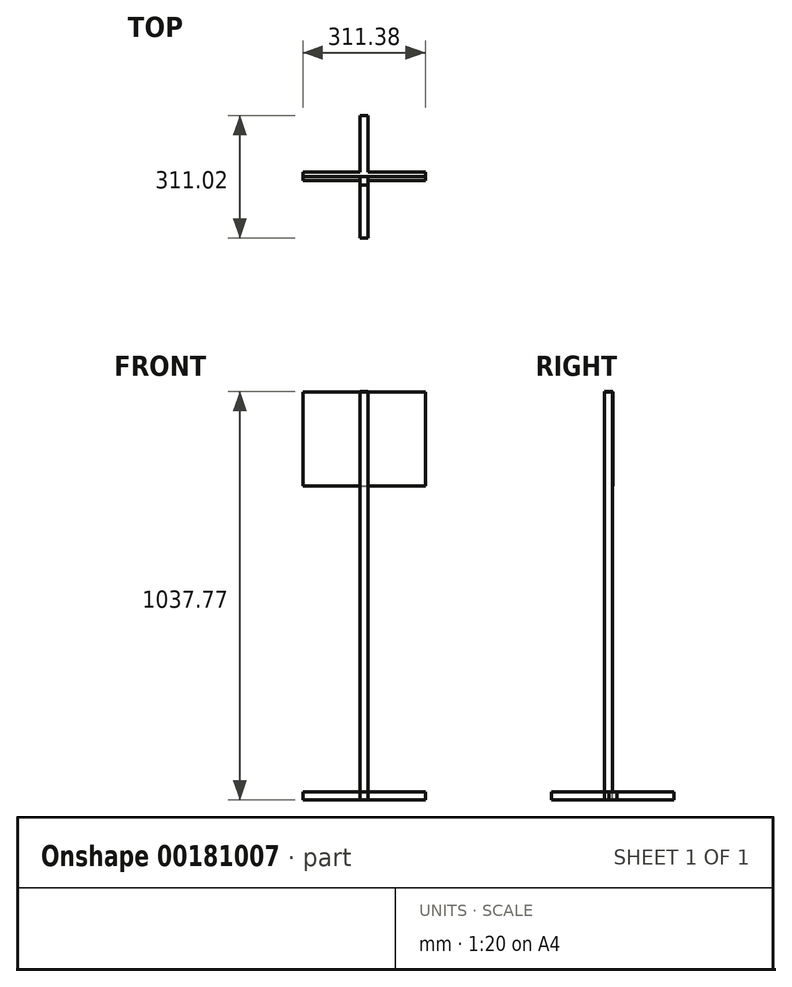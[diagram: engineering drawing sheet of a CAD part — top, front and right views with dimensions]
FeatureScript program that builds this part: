
annotation { "Feature Type Name" : "Feature", "Feature Type Description" : "" }
export const myFeature = defineFeature(function(context is Context, id is Id, definition is map)
    precondition{}
    {
        {
            var Q0;
            Q0=qCreatedBy(makeId("Front.planeOp"),FACE);
            var sketch = newSketch(context, id + "F0", { "sketchPlane" : qUnion([Q0])});
            skLineSegment(sketch, "E0.bottom", {"start": v(-155.15, 132.26) * mm, "end": v(155.87, 132.26) * mm});
            skLineSegment(sketch, "E0.top", {"start": v(-155.15, -106.2) * mm, "end": v(155.87, -106.2) * mm});
            skLineSegment(sketch, "E0.left", {"start": v(-155.15, 132.26) * mm, "end": v(-155.15, -106.2) * mm});
            skLineSegment(sketch, "E0.right", {"start": v(155.87, 132.26) * mm, "end": v(155.87, -106.2) * mm});
            skSolve(sketch);
        }
        {
            var Q0;
            Q0=makeQuery(id+"F0.imprint","IMPRINT",FACE,{"disambiguationData":[TD([[makeQuery(id+"F0.imprint","IMPRINT",EDGE,{"derivedFrom":sQuery(id+"F0.wireOp",EDGE,"E0.bottom")}),-1.0]])]});
            extrude(context, id + "F1", {"entities" : qUnion([Q0]), "depth" : 1 * mm});
        }
        {
            var Q0;
            Q0=makeQuery(id+"F1.opExtrude","CAP_FACE",FACE,{"disambiguationData":[OSD([sQuery(id+"F0.wireOp",EDGE,"E0.bottom"),sQuery(id+"F0.wireOp",EDGE,"E0.top"),sQuery(id+"F0.wireOp",EDGE,"E0.left"),sQuery(id+"F0.wireOp",EDGE,"E0.right")])],"isStart":false});
            var sketch = newSketch(context, id + "F2", { "sketchPlane" : qUnion([Q0])});
            skLineSegment(sketch, "E1.bottom", {"start": v(-10.37, 131.22) * mm, "end": v(10.37, 131.22) * mm});
            skLineSegment(sketch, "E1.top", {"start": v(-10.37, 133.3) * mm, "end": v(10.37, 133.3) * mm});
            skLineSegment(sketch, "E1.left", {"start": v(-10.37, 131.22) * mm, "end": v(-10.37, 133.3) * mm});
            skLineSegment(sketch, "E1.right", {"start": v(10.37, 131.22) * mm, "end": v(10.37, 133.3) * mm});
            skPoint(sketch, "E1.middle", {"position": v(0, 132.26) * mm});
            skSolve(sketch);
        }
        {
            var Q0;
            {var subQ0=sQuery(id+"F2.wireOp",EDGE,"E1.top");Q0=makeQuery(id+"F2.imprint","IMPRINT",FACE,{"disambiguationData":[TD([[makeQuery(id+"F2.imprint","IMPRINT",EDGE,{"derivedFrom":subQ0}),-1.0]])]});}
            extrude(context, id + "F3", {"entities" : qUnion([Q0]), "operationType" : NewBodyOperationType.ADD, "depth" : 20.73 * mm});
        }
        {
            var Q0;
            Q0=makeQuery(id+"F3.opExtrude","SWEPT_FACE",FACE,{"disambiguationData":[OSD([sQuery(id+"F0.wireOp",EDGE,"E0.bottom")])]});
            var sketch = newSketch(context, id + "F4", { "sketchPlane" : qUnion([Q0])});
            skLineSegment(sketch, "E2", {"start": v(-10.37, 21.73) * mm, "end": v(10.37, 21.73) * mm});
            skLineSegment(sketch, "E3", {"start": v(10.37, 21.73) * mm, "end": v(10.37, 1) * mm});
            skLineSegment(sketch, "E4", {"start": v(10.37, 1) * mm, "end": v(-10.37, 1) * mm});
            skLineSegment(sketch, "E5", {"start": v(-10.37, 1) * mm, "end": v(-10.37, 21.73) * mm});
            skSolve(sketch);
        }
        {
            var Q0;
            Q0=makeQuery(id+"F1.opExtrude","CAP_FACE",FACE,{"disambiguationData":[OSD([sQuery(id+"F0.wireOp",EDGE,"E0.bottom"),sQuery(id+"F0.wireOp",EDGE,"E0.top"),sQuery(id+"F0.wireOp",EDGE,"E0.left"),sQuery(id+"F0.wireOp",EDGE,"E0.right")])],"isStart":false});
            var sketch = newSketch(context, id + "F5", { "sketchPlane" : qUnion([Q0])});
            skLineSegment(sketch, "E6.bottom", {"start": v(10.37, -904.48) * mm, "end": v(-10.37, -904.48) * mm});
            skLineSegment(sketch, "E6.top", {"start": v(10.37, -883.74) * mm, "end": v(-10.37, -883.74) * mm});
            skLineSegment(sketch, "E6.left", {"start": v(10.37, -904.48) * mm, "end": v(10.37, -883.74) * mm});
            skLineSegment(sketch, "E6.right", {"start": v(-10.37, -904.48) * mm, "end": v(-10.37, -883.74) * mm});
            skPoint(sketch, "E6.middle", {"position": v(0, -894.1) * mm});
            skSolve(sketch);
        }
        {
            var Q0;
            Q0=makeQuery(id+"F5.imprint","IMPRINT",FACE,{"disambiguationData":[TD([[makeQuery(id+"F5.imprint","IMPRINT",EDGE,{"derivedFrom":sQuery(id+"F5.wireOp",EDGE,"E6.bottom")}),-1.0]])]});
            extrude(context, id + "F6", {"entities" : qUnion([Q0]), "endBound" : BoundingType.SYMMETRIC, "depth" : 311.02 * mm});
        }
        {
            var Q0;
            Q0=qCreatedBy(makeId("Right.planeOp"),FACE);
            var sketch = newSketch(context, id + "F7", { "sketchPlane" : qUnion([Q0])});
            skLineSegment(sketch, "E7.bottom", {"start": v(-10.37, -883.74) * mm, "end": v(10.37, -883.74) * mm});
            skLineSegment(sketch, "E7.top", {"start": v(-10.37, -904.48) * mm, "end": v(10.37, -904.48) * mm});
            skLineSegment(sketch, "E7.left", {"start": v(-10.37, -883.74) * mm, "end": v(-10.37, -904.48) * mm});
            skLineSegment(sketch, "E7.right", {"start": v(10.37, -883.74) * mm, "end": v(10.37, -904.48) * mm});
            skPoint(sketch, "E7.middle", {"position": v(0, -894.1) * mm});
            skSolve(sketch);
        }
        {
            var Q0;
            Q0 = qSketchRegion(id + "F7", true);
            extrude(context, id + "F8", {"entities" : qUnion([Q0]), "operationType" : NewBodyOperationType.ADD, "endBound" : BoundingType.SYMMETRIC, "depth" : 311.02 * mm});
        }
        {
            var Q0;
            Q0=makeQuery(id+"F4.imprint","IMPRINT",FACE,{"disambiguationData":[TD([[makeQuery(id+"F4.imprint","IMPRINT",EDGE,{"derivedFrom":sQuery(id+"F4.wireOp",EDGE,"E2")}),-1.0]])]});
            extrude(context, id + "F9", {"entities" : qUnion([Q0]), "depth" : 1036.73 * mm});
        }
        {
            var Q0;
            Q0=makeQuery(id+"F0.imprint","IMPRINT",FACE,{"disambiguationData":[TD([[makeQuery(id+"F0.imprint","IMPRINT",EDGE,{"derivedFrom":sQuery(id+"F0.wireOp",EDGE,"E0.bottom")}),-1.0]])]});
            var sketch = newSketch(context, id + "F10", { "sketchPlane" : qUnion([Q0])});
            skCircle(sketch, "E8", {"center": v(111.7, 93.2) * mm, "radius": 145.48 * mm});
            skPoint(sketch, "E8.first.point", {"position": v(0, 0) * mm});
            skPoint(sketch, "E8.second.point", {"position": v(223.4, 0) * mm});
            skPoint(sketch, "E8.third.point", {"position": v(0, 186.41) * mm});
            skCircle(sketch, "E9", {"center": v(-211.01, -200.4) * mm, "radius": 212.98 * mm});
            skPoint(sketch, "E9.first.point", {"position": v(-138.88, 0) * mm});
            skPoint(sketch, "E9.second.point", {"position": v(-283.14, 0) * mm});
            skPoint(sketch, "E9.third.point", {"position": v(0, -229.29) * mm});
            skSolve(sketch);
        }
        {
            var Q0;
            Q0=sQuery(id+"F10.wireOp",EDGE,"E9");
            extrude(context, id + "F11", {"bodyType" : ToolBodyType.SURFACE, "surfaceEntities" : qUnion([Q0]), "depth" : 10 * mm});
        }
    });
